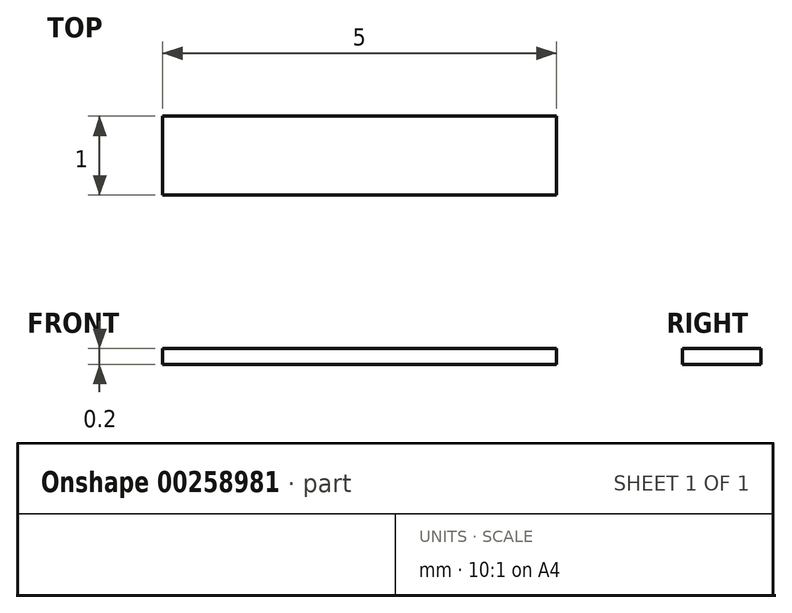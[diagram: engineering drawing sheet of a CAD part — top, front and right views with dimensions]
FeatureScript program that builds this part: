
annotation { "Feature Type Name" : "Feature", "Feature Type Description" : "" }
export const myFeature = defineFeature(function(context is Context, id is Id, definition is map)
    precondition{}
    {
        {
            var Q0;
            Q0=qCreatedBy(makeId("Top.planeOp"),FACE);
            var sketch = newSketch(context, id + "F0", { "sketchPlane" : qUnion([Q0])});
            skLineSegment(sketch, "E0.bottom", {"start": v(0, 0) * mm, "end": v(5, 0) * mm});
            skLineSegment(sketch, "E0.top", {"start": v(0, 1) * mm, "end": v(5, 1) * mm});
            skLineSegment(sketch, "E0.left", {"start": v(0, 0) * mm, "end": v(0, 1) * mm});
            skLineSegment(sketch, "E0.right", {"start": v(5, 0) * mm, "end": v(5, 1) * mm});
            skSolve(sketch);
        }
        {
            var Q0;
            Q0 = qSketchRegion(id + "F0", true);
            extrude(context, id + "F1", {"entities" : qUnion([Q0]), "depth" : .2 * mm});
        }
    });
